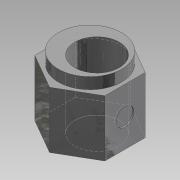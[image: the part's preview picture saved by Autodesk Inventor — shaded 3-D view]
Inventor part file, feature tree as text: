
AUTODESK INVENTOR PART (.ipt)
format: ipt  version: 2013 SP2 (Build 170200200, 200)  size: 110,080 bytes
history: native  units: mm
features: extrude x3, sketch x3
ambient origin geometry x8: Origin, YZ Plane, XZ Plane, XY Plane, X Axis, Y Axis, Z Axis, Center Point
bodies: Solid1 (feature_tree)
feature tree (6):
  extrude  "Extrusion1"  Depth=0.79mm
  extrude  "Extrusion2"  Depth=6.35mm TaperAngle=0.0deg
  extrude  "Extrusion3"  Depth=1.27mm TaperAngle=0.0deg
  sketch  "Sketch1"  dims[d0=7.87mm d1=0.79mm]
  sketch  "Sketch2"  dims[d2=5.0mm d3=6.35mm d4=0.0mm]
  sketch  "Sketch3"  dims[d5=7.11mm d6=1.27mm d7=0.0mm d8=2.0mm d9=0.15mm d10=0.0mm]
